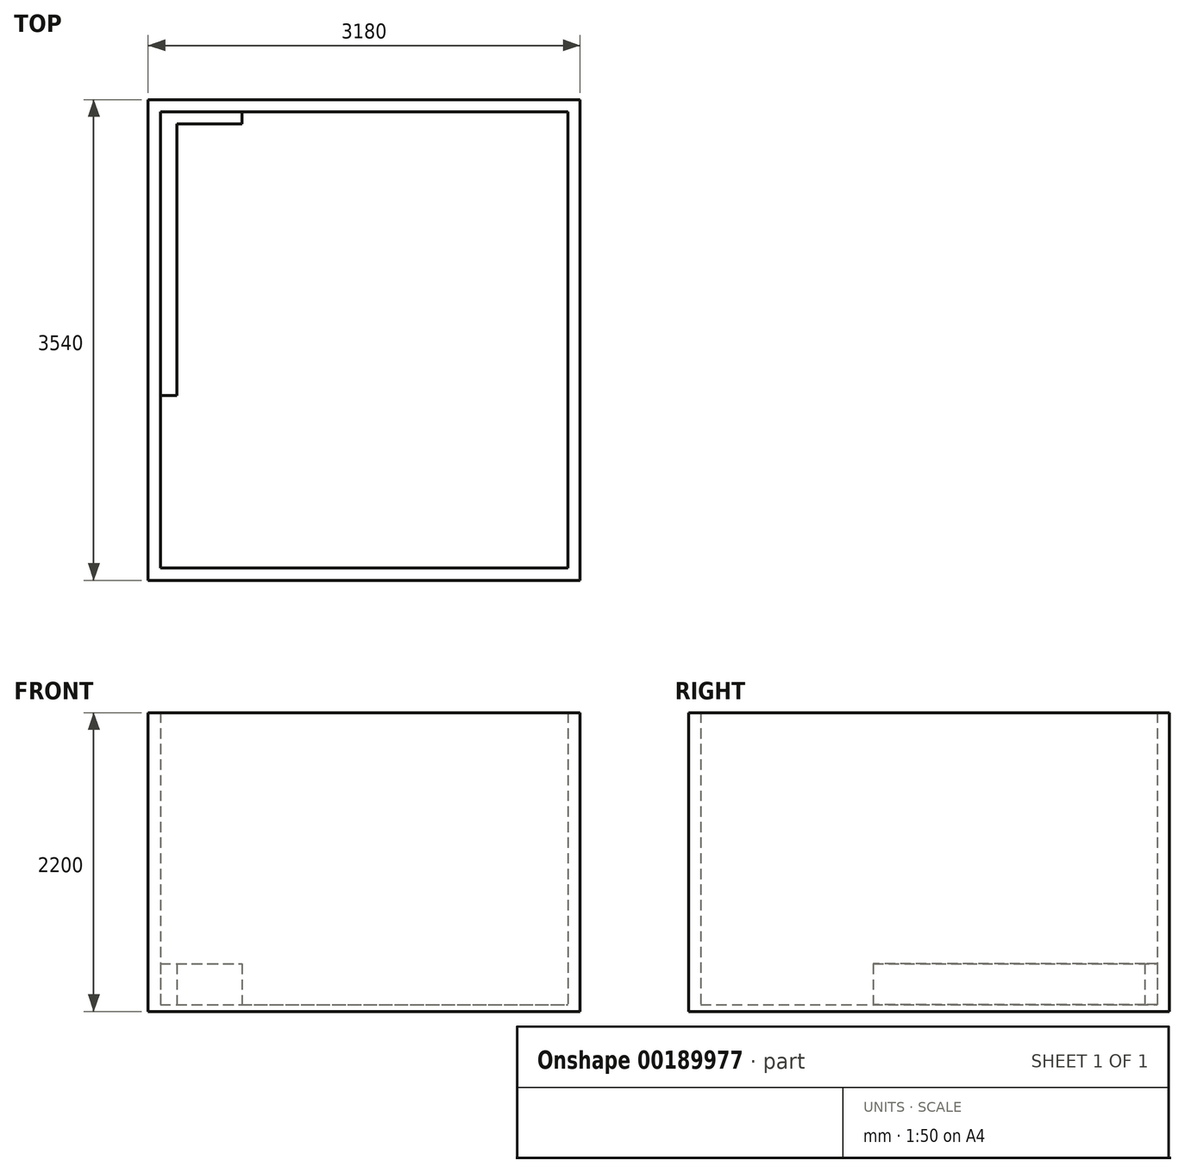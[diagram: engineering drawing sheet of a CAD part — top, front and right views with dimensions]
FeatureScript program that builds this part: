
annotation { "Feature Type Name" : "Feature", "Feature Type Description" : "" }
export const myFeature = defineFeature(function(context is Context, id is Id, definition is map)
    precondition{}
    {
        {
            var Q0;
            Q0=qCreatedBy(makeId("Top.planeOp"),FACE);
            var sketch = newSketch(context, id + "F0", { "sketchPlane" : qUnion([Q0])});
            skLineSegment(sketch, "E0.bottom", {"start": v(-1497.27, -1822.55) * mm, "end": v(1502.73, -1822.55) * mm});
            skLineSegment(sketch, "E0.top", {"start": v(-1497.27, 1537.45) * mm, "end": v(1502.73, 1537.45) * mm});
            skLineSegment(sketch, "E0.left", {"start": v(-1497.27, -1822.55) * mm, "end": v(-1497.27, 1537.45) * mm});
            skLineSegment(sketch, "E0.right", {"start": v(1502.73, -1822.55) * mm, "end": v(1502.73, 1537.45) * mm});
            skSolve(sketch);
        }
        {
            var Q0;
            Q0 = qSketchRegion(id + "F0", true);
            extrude(context, id + "F1", {"entities" : qUnion([Q0]), "oppositeDirection" : true, "depth" : 50 * mm});
        }
        {
            var Q0;
            Q0=makeQuery(id+"F1.opExtrude","CAP_FACE",FACE,{"disambiguationData":[OSD([sQuery(id+"F0.wireOp",EDGE,"E0.bottom"),sQuery(id+"F0.wireOp",EDGE,"E0.top"),sQuery(id+"F0.wireOp",EDGE,"E0.left"),sQuery(id+"F0.wireOp",EDGE,"E0.right")])],"isStart":true});
            var sketch = newSketch(context, id + "F2", { "sketchPlane" : qUnion([Q0])});
            skLineSegment(sketch, "E1.bottom", {"start": v(-1497.27, 1537.45) * mm, "end": v(-897.27, 1537.45) * mm});
            skLineSegment(sketch, "E1.top", {"start": v(-1497.27, 1447.45) * mm, "end": v(-897.27, 1447.45) * mm});
            skLineSegment(sketch, "E1.left", {"start": v(-1497.27, 1537.45) * mm, "end": v(-1497.27, 1447.45) * mm});
            skLineSegment(sketch, "E1.right", {"start": v(-897.27, 1537.45) * mm, "end": v(-897.27, 1447.45) * mm});
            skSolve(sketch);
        }
        {
            var Q0;
            Q0 = qSketchRegion(id + "F2", true);
            extrude(context, id + "F3", {"entities" : qUnion([Q0]), "operationType" : NewBodyOperationType.ADD, "depth" : 300 * mm});
        }
        {
            var Q0;
            Q0=makeQuery(id+"F3.opExtrude","SWEPT_FACE",FACE,{"disambiguationData":[OSD([sQuery(id+"F2.wireOp",EDGE,"E1.top")])]});
            var sketch = newSketch(context, id + "F4", { "sketchPlane" : qUnion([Q0])});
            skCircle(sketch, "E2", {"center": v(-1447.27, 240) * mm, "radius": 12.5 * mm});
            skSolve(sketch);
        }
        {
            var Q0;
            Q0=makeQuery(id+"F3.boolean.opBoolean","MERGE",FACE,{"derivedFrom":[makeQuery(id+"F1.opExtrude","SWEPT_FACE",FACE,{"disambiguationData":[OSD([sQuery(id+"F0.wireOp",EDGE,"E0.left")])]}),makeQuery(id+"F3.opExtrude","SWEPT_FACE",FACE,{"disambiguationData":[OSD([sQuery(id+"F2.wireOp",EDGE,"E1.left")])]})]});
            cPlane(context, id + "F5", {"entities" : qUnion([Q0]), "cplaneType" : CPlaneType.OFFSET, "offset" : 50 * mm, "oppositeDirection" : true, "width" : 150 * mm, "height" : 150 * mm});
        }
        {
            var Q0;
            Q0=qCreatedBy(id+"F5.planeOp",FACE);
            var sketch = newSketch(context, id + "F6", { "sketchPlane" : qUnion([Q0])});
            skLineSegment(sketch, "E3", {"start": v(-1447.45, 240) * mm, "end": v(-397.45, 240) * mm});
            skLineSegment(sketch, "E4", {"start": v(-397.45, 240) * mm, "end": v(-397.45, 540) * mm});
            skSolve(sketch);
        }
        {
            var Q0;
            Q0=makeQuery(id+"F1.opExtrude","CAP_FACE",FACE,{"disambiguationData":[OSD([sQuery(id+"F0.wireOp",EDGE,"E0.bottom"),sQuery(id+"F0.wireOp",EDGE,"E0.top"),sQuery(id+"F0.wireOp",EDGE,"E0.left"),sQuery(id+"F0.wireOp",EDGE,"E0.right")])],"isStart":true});
            var sketch = newSketch(context, id + "F7", { "sketchPlane" : qUnion([Q0])});
            skLineSegment(sketch, "E5.bottom", {"start": v(-1497.27, 1447.45) * mm, "end": v(-1377.27, 1447.45) * mm});
            skLineSegment(sketch, "E5.top", {"start": v(-1497.27, -552.55) * mm, "end": v(-1377.27, -552.55) * mm});
            skLineSegment(sketch, "E5.left", {"start": v(-1497.27, 1447.45) * mm, "end": v(-1497.27, -552.55) * mm});
            skLineSegment(sketch, "E5.right", {"start": v(-1377.27, 1447.45) * mm, "end": v(-1377.27, -552.55) * mm});
            skSolve(sketch);
        }
        {
            var Q0;
            Q0 = qSketchRegion(id + "F7", true);
            extrude(context, id + "F8", {"entities" : qUnion([Q0]), "operationType" : NewBodyOperationType.ADD, "depth" : 300 * mm});
        }
        {
            var Q0;
            Q0=makeQuery(id+"F1.opExtrude","CAP_FACE",FACE,{"disambiguationData":[OSD([sQuery(id+"F0.wireOp",EDGE,"E0.bottom"),sQuery(id+"F0.wireOp",EDGE,"E0.top"),sQuery(id+"F0.wireOp",EDGE,"E0.left"),sQuery(id+"F0.wireOp",EDGE,"E0.right")])],"isStart":false});
            cPlane(context, id + "F9", {"entities" : qUnion([Q0]), "cplaneType" : CPlaneType.OFFSET, "offset" : 0 * mm, "width" : 150 * mm, "height" : 150 * mm});
        }
        {
            var Q0;
            Q0=qCreatedBy(id+"F9.planeOp",FACE);
            var sketch = newSketch(context, id + "F10", { "sketchPlane" : qUnion([Q0])});
            skLineSegment(sketch, "E6.left", {"start": v(1592.73, 1912.55) * mm, "end": v(1592.73, -1627.45) * mm});
            skLineSegment(sketch, "E6.right", {"start": v(1502.73, 1822.55) * mm, "end": v(1502.73, -1537.45) * mm});
            skLineSegment(sketch, "E7.bottom", {"start": v(1502.73, -1537.45) * mm, "end": v(-1497.27, -1537.45) * mm});
            skLineSegment(sketch, "E7.top", {"start": v(1592.73, -1627.45) * mm, "end": v(-1587.27, -1627.45) * mm});
            skLineSegment(sketch, "E8.left", {"start": v(-1497.27, -1537.45) * mm, "end": v(-1497.27, 1822.55) * mm});
            skLineSegment(sketch, "E8.right", {"start": v(-1587.27, -1627.45) * mm, "end": v(-1587.27, 1912.55) * mm});
            skLineSegment(sketch, "E9.bottom", {"start": v(1502.73, 1822.55) * mm, "end": v(-1497.27, 1822.55) * mm});
            skLineSegment(sketch, "E9.top", {"start": v(1593.03, 1912.55) * mm, "end": v(-1647.17, 1912.55) * mm});
            skSolve(sketch);
        }
        {
            var Q0;
            Q0 = qSketchRegion(id + "F10", true);
            extrude(context, id + "F11", {"entities" : qUnion([Q0]), "operationType" : NewBodyOperationType.ADD, "oppositeDirection" : true, "depth" : 2200 * mm});
        }
    });
